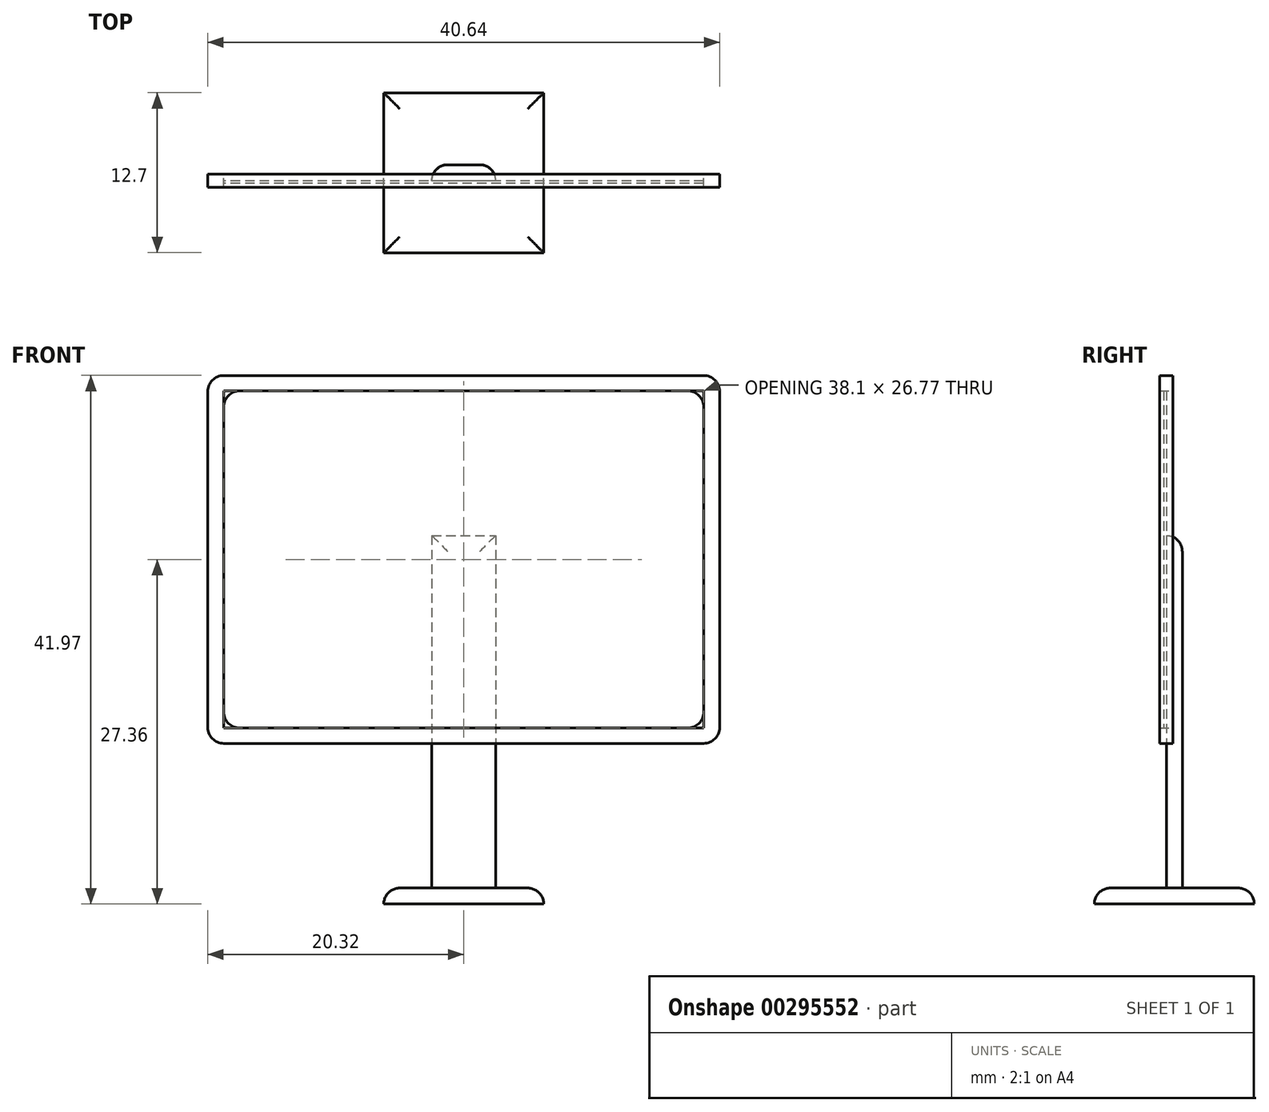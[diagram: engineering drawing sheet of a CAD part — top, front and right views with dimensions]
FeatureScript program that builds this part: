
annotation { "Feature Type Name" : "Feature", "Feature Type Description" : "" }
export const myFeature = defineFeature(function(context is Context, id is Id, definition is map)
    precondition{}
    {
        {
            var Q0;
            Q0=qCreatedBy(makeId("Front.planeOp"),FACE);
            var sketch = newSketch(context, id + "F0", { "sketchPlane" : qUnion([Q0])});
            skLineSegment(sketch, "E0.bottom", {"start": v(19.05, 13.39) * mm, "end": v(-19.05, 13.39) * mm});
            skLineSegment(sketch, "E0.top", {"start": v(19.05, -13.39) * mm, "end": v(-19.05, -13.39) * mm});
            skLineSegment(sketch, "E0.left", {"start": v(19.05, 13.39) * mm, "end": v(19.05, -13.39) * mm});
            skLineSegment(sketch, "E0.right", {"start": v(-19.05, 13.39) * mm, "end": v(-19.05, -13.39) * mm});
            skPoint(sketch, "E0.middle", {"position": v(0, 0) * mm});
            skLineSegment(sketch, "E1.bottom", {"start": v(20.32, 14.6) * mm, "end": v(-20.32, 14.6) * mm});
            skLineSegment(sketch, "E1.top", {"start": v(20.32, -14.6) * mm, "end": v(-20.32, -14.6) * mm});
            skLineSegment(sketch, "E1.left", {"start": v(20.32, 14.6) * mm, "end": v(20.32, -14.6) * mm});
            skLineSegment(sketch, "E1.right", {"start": v(-20.32, 14.6) * mm, "end": v(-20.32, -14.6) * mm});
            skSolve(sketch);
        }
        {
            var Q0;
            Q0=makeQuery(id+"F0.imprint","IMPRINT",FACE,{"disambiguationData":[TD([[makeQuery(id+"F0.imprint","IMPRINT",EDGE,{"derivedFrom":sQuery(id+"F0.wireOp",EDGE,"E0.bottom")}),1.0]])]});
            extrude(context, id + "F1", {"entities" : qUnion([Q0]), "depth" : 0.2 * mm});
        }
        {
            var Q0;
            Q0=makeQuery(id+"F0.imprint","IMPRINT",FACE,{"disambiguationData":[TD([[makeQuery(id+"F0.imprint","IMPRINT",EDGE,{"derivedFrom":sQuery(id+"F0.wireOp",EDGE,"E0.bottom")}),-1.0]])]});
            extrude(context, id + "F2", {"entities" : qUnion([Q0]), "endBound" : BoundingType.SYMMETRIC, "depth" : 1.07 * mm});
        }
        {
            var Q0;
            Q0=makeQuery(id+"F1.opExtrude","CAP_FACE",FACE,{"disambiguationData":[OSD([sQuery(id+"F0.wireOp",EDGE,"E0.bottom"),sQuery(id+"F0.wireOp",EDGE,"E0.top"),sQuery(id+"F0.wireOp",EDGE,"E0.left"),sQuery(id+"F0.wireOp",EDGE,"E0.right")])],"isStart":true});
            var sketch = newSketch(context, id + "F3", { "sketchPlane" : qUnion([Q0])});
            skLineSegment(sketch, "E2.bottom", {"start": v(2.54, 1.9) * mm, "end": v(-2.54, 1.9) * mm});
            skLineSegment(sketch, "E2.top", {"start": v(2.54, -1.9) * mm, "end": v(-2.54, -1.9) * mm});
            skLineSegment(sketch, "E2.left", {"start": v(2.54, 1.9) * mm, "end": v(2.54, -1.9) * mm});
            skLineSegment(sketch, "E2.right", {"start": v(-2.54, 1.9) * mm, "end": v(-2.54, -1.9) * mm});
            skPoint(sketch, "E2.middle", {"position": v(0, 0) * mm});
            skLineSegment(sketch, "E3.bottom", {"start": v(-2.54, -1.9) * mm, "end": v(2.54, -1.9) * mm});
            skLineSegment(sketch, "E3.top", {"start": v(-2.54, -13.39) * mm, "end": v(2.54, -13.39) * mm});
            skLineSegment(sketch, "E3.left", {"start": v(-2.54, -1.9) * mm, "end": v(-2.54, -13.39) * mm});
            skLineSegment(sketch, "E3.right", {"start": v(2.54, -1.9) * mm, "end": v(2.54, -13.39) * mm});
            skLineSegment(sketch, "E4.top", {"start": v(-2.54, -26.09) * mm, "end": v(2.54, -26.09) * mm});
            skLineSegment(sketch, "E4.left", {"start": v(-2.54, -13.39) * mm, "end": v(-2.54, -26.09) * mm});
            skLineSegment(sketch, "E4.right", {"start": v(2.54, -13.39) * mm, "end": v(2.54, -26.09) * mm});
            skSolve(sketch);
        }
        {
            var Q0;
            Q0 = qSketchRegion(id + "F3", true);
            extrude(context, id + "F4", {"entities" : qUnion([Q0]), "depth" : 1.27 * mm});
        }
        {
            var Q0;
            Q0=makeQuery(id+"F4.opExtrude","SWEPT_FACE",FACE,{"disambiguationData":[OSD([sQuery(id+"F3.wireOp",EDGE,"E4.top")])]});
            var sketch = newSketch(context, id + "F5", { "sketchPlane" : qUnion([Q0])});
            skLineSegment(sketch, "E5", {"start": v(0, 0) * mm, "end": v(0, -1.27) * mm});
            skPoint(sketch, "E6", {"position": v(0, -0.64) * mm});
            skLineSegment(sketch, "E7.bottom", {"start": v(6.35, 5.71) * mm, "end": v(-6.35, 5.72) * mm});
            skLineSegment(sketch, "E7.top", {"start": v(6.35, -6.99) * mm, "end": v(-6.35, -6.98) * mm});
            skLineSegment(sketch, "E7.left", {"start": v(6.35, 5.71) * mm, "end": v(6.35, -6.99) * mm});
            skLineSegment(sketch, "E7.right", {"start": v(-6.35, 5.72) * mm, "end": v(-6.35, -6.99) * mm});
            skSolve(sketch);
        }
        {
            var Q0;
            Q0 = qSketchRegion(id + "F5", true);
            extrude(context, id + "F6", {"entities" : qUnion([Q0]), "operationType" : NewBodyOperationType.ADD, "depth" : 1.27 * mm});
        }
        {
            var Q0;
            Q0=makeQuery(id+"F4.opExtrude","CAP_EDGE",EDGE,{"disambiguationData":[OSD([sQuery(id+"F3.wireOp",EDGE,"E4.top")])],"isStart":true});
            var Q1;
            Q1=makeQuery(id+"F4.opExtrude","SWEPT_EDGE",EDGE,{"disambiguationData":[OSD([sQuery(id+"F3.wireOp",EDGE,"E4.top"),sQuery(id+"F3.wireOp",EDGE,"E4.right")])]});
            var Q2;
            Q2=makeQuery(id+"F4.opExtrude","SWEPT_EDGE",EDGE,{"disambiguationData":[OSD([sQuery(id+"F3.wireOp",EDGE,"E4.top"),sQuery(id+"F3.wireOp",EDGE,"E4.left")])]});
            var Q3;
            Q3=makeQuery(id+"F4.opExtrude","CAP_EDGE",EDGE,{"disambiguationData":[OSD([sQuery(id+"F3.wireOp",EDGE,"E4.top")])],"isStart":false});
            var Q4;
            Q4=makeQuery(id+"F6.opExtrude","CAP_EDGE",EDGE,{"disambiguationData":[OSD([sQuery(id+"F5.wireOp",EDGE,"E7.top")])],"isStart":true});
            var Q5;
            Q5=makeQuery(id+"F6.opExtrude","CAP_EDGE",EDGE,{"disambiguationData":[OSD([sQuery(id+"F5.wireOp",EDGE,"E7.left")])],"isStart":true});
            var Q6;
            Q6=makeQuery(id+"F6.opExtrude","CAP_EDGE",EDGE,{"disambiguationData":[OSD([sQuery(id+"F5.wireOp",EDGE,"E7.bottom")])],"isStart":true});
            var Q7;
            Q7=makeQuery(id+"F6.opExtrude","CAP_EDGE",EDGE,{"disambiguationData":[OSD([sQuery(id+"F5.wireOp",EDGE,"E7.right")])],"isStart":true});
            var Q8;
            Q8=makeQuery(id+"F4.opExtrude","CAP_EDGE",EDGE,{"disambiguationData":[OSD([sQuery(id+"F3.wireOp",EDGE,"E2.right"),sQuery(id+"F3.wireOp",EDGE,"E3.left"),sQuery(id+"F3.wireOp",EDGE,"E4.left")])],"isStart":false});
            var Q9;
            Q9=makeQuery(id+"F4.opExtrude","CAP_EDGE",EDGE,{"disambiguationData":[OSD([sQuery(id+"F3.wireOp",EDGE,"E2.left"),sQuery(id+"F3.wireOp",EDGE,"E3.right"),sQuery(id+"F3.wireOp",EDGE,"E4.right")])],"isStart":false});
            var Q10;
            Q10=makeQuery(id+"F4.opExtrude","CAP_EDGE",EDGE,{"disambiguationData":[OSD([sQuery(id+"F3.wireOp",EDGE,"E2.bottom")])],"isStart":false});
            var Q11;
            Q11=makeQuery(id+"F2.opExtrude","SWEPT_EDGE",EDGE,{"disambiguationData":[OSD([sQuery(id+"F0.wireOp",EDGE,"E1.top"),sQuery(id+"F0.wireOp",EDGE,"E1.right")])]});
            var Q12;
            Q12=makeQuery(id+"F2.opExtrude","SWEPT_EDGE",EDGE,{"disambiguationData":[OSD([sQuery(id+"F0.wireOp",EDGE,"E1.top"),sQuery(id+"F0.wireOp",EDGE,"E1.left")])]});
            var Q13;
            Q13=makeQuery(id+"F2.opExtrude","SWEPT_EDGE",EDGE,{"disambiguationData":[OSD([sQuery(id+"F0.wireOp",EDGE,"E1.bottom"),sQuery(id+"F0.wireOp",EDGE,"E1.right")])]});
            var Q14;
            Q14=makeQuery(id+"F2.opExtrude","SWEPT_EDGE",EDGE,{"disambiguationData":[OSD([sQuery(id+"F0.wireOp",EDGE,"E1.bottom"),sQuery(id+"F0.wireOp",EDGE,"E1.left")])]});
            fillet(context, id + "F7", {"entities" : qUnion([Q0, Q1, Q2, Q3, Q4, Q5, Q6, Q7, Q8, Q9, Q10, Q11, Q12, Q13, Q14]), "radius" : 1.27 * mm, "tangentPropagation" : true, "allowEdgeOverflow" : false});
        }
        {
            var Q0;
            Q0=makeQuery(id+"F2.opExtrude","SWEPT_EDGE",EDGE,{"disambiguationData":[OSD([sQuery(id+"F0.wireOp",EDGE,"E0.bottom"),sQuery(id+"F0.wireOp",EDGE,"E0.right")])]});
            var Q1;
            Q1=makeQuery(id+"F2.opExtrude","SWEPT_EDGE",EDGE,{"disambiguationData":[OSD([sQuery(id+"F0.wireOp",EDGE,"E0.bottom"),sQuery(id+"F0.wireOp",EDGE,"E0.left")])]});
            var Q2;
            Q2=makeQuery(id+"F2.opExtrude","SWEPT_EDGE",EDGE,{"disambiguationData":[OSD([sQuery(id+"F0.wireOp",EDGE,"E0.top"),sQuery(id+"F0.wireOp",EDGE,"E0.right")])]});
            var Q3;
            Q3=makeQuery(id+"F2.opExtrude","SWEPT_EDGE",EDGE,{"disambiguationData":[OSD([sQuery(id+"F0.wireOp",EDGE,"E0.top"),sQuery(id+"F0.wireOp",EDGE,"E0.left")])]});
            fillet(context, id + "F8", {"entities" : qUnion([Q0, Q1, Q2, Q3]), "radius" : 1.27 * mm, "tangentPropagation" : true, "allowEdgeOverflow" : false});
        }
    });
